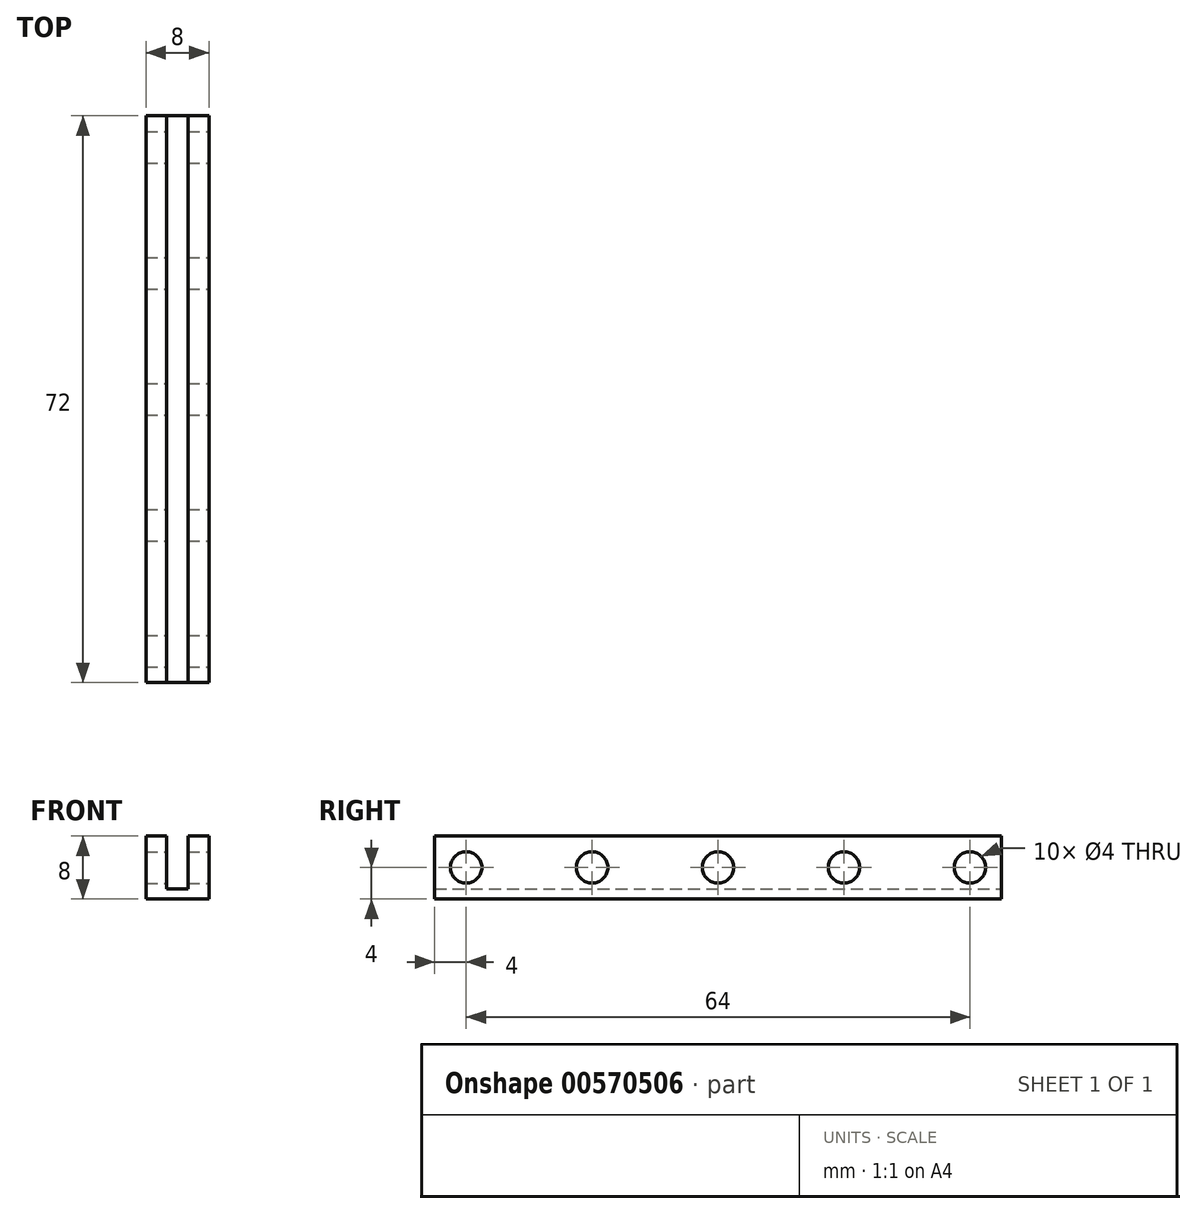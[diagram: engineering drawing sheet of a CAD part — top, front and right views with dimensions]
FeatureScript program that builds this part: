
annotation { "Feature Type Name" : "Feature", "Feature Type Description" : "" }
export const myFeature = defineFeature(function(context is Context, id is Id, definition is map)
    precondition{}
    {
        {
            var Q0;
            Q0=qCreatedBy(makeId("Front.planeOp"),FACE);
            var sketch = newSketch(context, id + "F0", { "sketchPlane" : qUnion([Q0])});
            skLineSegment(sketch, "E0.bottom", {"start": v(-4, 4) * mm, "end": v(4, 4) * mm});
            skLineSegment(sketch, "E0.top", {"start": v(-4, -4) * mm, "end": v(4, -4) * mm});
            skLineSegment(sketch, "E0.left", {"start": v(-4, 4) * mm, "end": v(-4, -4) * mm});
            skLineSegment(sketch, "E0.right", {"start": v(4, 4) * mm, "end": v(4, -4) * mm});
            skPoint(sketch, "E0.middle", {"position": v(0, 0) * mm});
            skLineSegment(sketch, "E1.bottom", {"start": v(-1.34, 10.75) * mm, "end": v(1.34, 10.75) * mm});
            skLineSegment(sketch, "E1.top", {"start": v(-1.34, -2.75) * mm, "end": v(1.34, -2.75) * mm});
            skLineSegment(sketch, "E1.left", {"start": v(-1.34, 10.75) * mm, "end": v(-1.34, -2.75) * mm});
            skLineSegment(sketch, "E1.right", {"start": v(1.34, 10.75) * mm, "end": v(1.34, -2.75) * mm});
            skPoint(sketch, "E1.middle", {"position": v(0, 4) * mm});
            skSolve(sketch);
        }
        {
            var Q0;
            Q0=makeQuery(id+"F0.imprint","IMPRINT",FACE,{"disambiguationData":[TD([[makeQuery(id+"F0.imprint","IMPRINT",EDGE,{"derivedFrom":sQuery(id+"F0.wireOp",EDGE,"E0.top")}),1.0]])]});
            extrude(context, id + "F1", {"entities" : qUnion([Q0]), "depth" : 72 * mm, "offsetDistance" : 25 * mm});
        }
        {
            var Q0;
            Q0=makeQuery(id+"F1.opExtrude","SWEPT_FACE",FACE,{"disambiguationData":[OSD([sQuery(id+"F0.wireOp",EDGE,"E0.right")])]});
            var sketch = newSketch(context, id + "F2", { "sketchPlane" : qUnion([Q0])});
            skCircle(sketch, "E2", {"center": v(-68, 0) * mm, "radius": 2 * mm});
            skCircle(sketch, "E3", {"center": v(-52, 0) * mm, "radius": 2 * mm});
            skCircle(sketch, "E4", {"center": v(-36, 0) * mm, "radius": 2 * mm});
            skCircle(sketch, "E5", {"center": v(-20, 0) * mm, "radius": 2 * mm});
            skCircle(sketch, "E6", {"center": v(-4, 0) * mm, "radius": 2 * mm});
            skSolve(sketch);
        }
        {
            var Q0;
            Q0=makeQuery(id+"F2.imprint","IMPRINT",FACE,{"disambiguationData":[TD([[makeQuery(id+"F2.imprint","IMPRINT",EDGE,{"derivedFrom":sQuery(id+"F2.wireOp",EDGE,"E2")}),1.0]])]});
            var Q1;
            Q1=makeQuery(id+"F2.imprint","IMPRINT",FACE,{"disambiguationData":[TD([[makeQuery(id+"F2.imprint","IMPRINT",EDGE,{"derivedFrom":sQuery(id+"F2.wireOp",EDGE,"E3")}),1.0]])]});
            var Q2;
            Q2=makeQuery(id+"F2.imprint","IMPRINT",FACE,{"disambiguationData":[TD([[makeQuery(id+"F2.imprint","IMPRINT",EDGE,{"derivedFrom":sQuery(id+"F2.wireOp",EDGE,"E4")}),1.0]])]});
            var Q3;
            Q3=makeQuery(id+"F2.imprint","IMPRINT",FACE,{"disambiguationData":[TD([[makeQuery(id+"F2.imprint","IMPRINT",EDGE,{"derivedFrom":sQuery(id+"F2.wireOp",EDGE,"E5")}),1.0]])]});
            var Q4;
            Q4=makeQuery(id+"F2.imprint","IMPRINT",FACE,{"disambiguationData":[TD([[makeQuery(id+"F2.imprint","IMPRINT",EDGE,{"derivedFrom":sQuery(id+"F2.wireOp",EDGE,"E6")}),1.0]])]});
            extrude(context, id + "F3", {"entities" : qUnion([Q0, Q1, Q2, Q3, Q4]), "operationType" : NewBodyOperationType.REMOVE, "oppositeDirection" : true, "depth" : 8.1 * mm, "offsetDistance" : 25 * mm});
        }
    });
